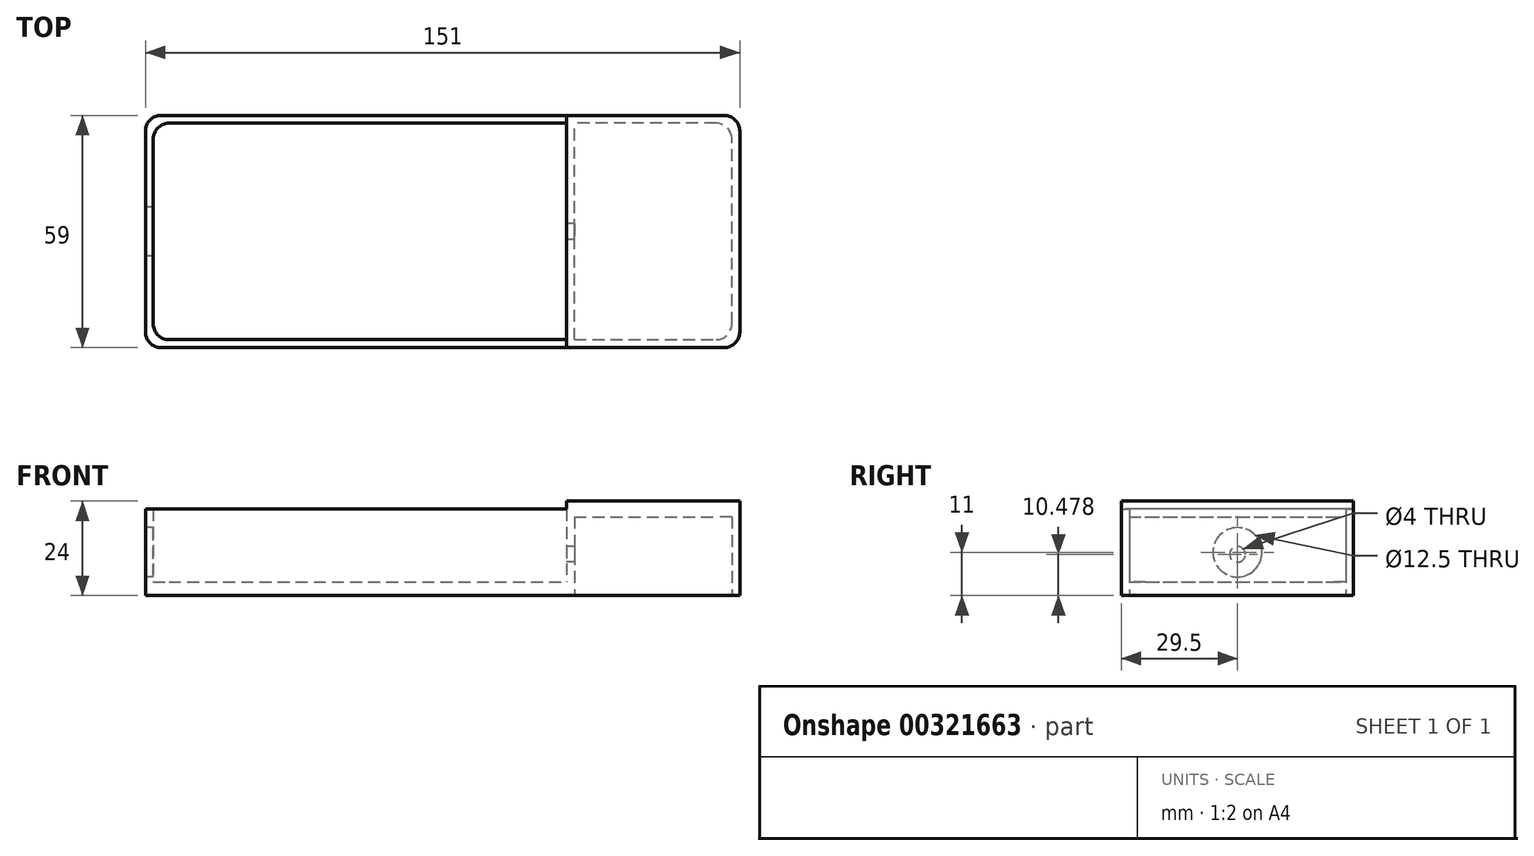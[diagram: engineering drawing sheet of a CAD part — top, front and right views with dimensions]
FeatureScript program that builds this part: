
annotation { "Feature Type Name" : "Feature", "Feature Type Description" : "" }
export const myFeature = defineFeature(function(context is Context, id is Id, definition is map)
    precondition{}
    {
        {
            var Q0;
            Q0=qCreatedBy(makeId("Top.planeOp"),FACE);
            var sketch = newSketch(context, id + "F0", { "sketchPlane" : qUnion([Q0])});
            skLineSegment(sketch, "E0.bottom", {"start": v(65.5, 29.5) * mm, "end": v(-65.5, 29.5) * mm});
            skLineSegment(sketch, "E0.top", {"start": v(65.5, -29.5) * mm, "end": v(-65.5, -29.5) * mm});
            skLineSegment(sketch, "E0.left", {"start": v(65.5, 29.5) * mm, "end": v(65.5, -29.5) * mm});
            skLineSegment(sketch, "E0.right", {"start": v(-65.5, 29.5) * mm, "end": v(-65.5, -29.5) * mm});
            skPoint(sketch, "E0.middle", {"position": v(0, 0) * mm});
            skLineSegment(sketch, "E1.bottom", {"start": v(-63.5, 27.5) * mm, "end": v(21.5, 27.5) * mm});
            skLineSegment(sketch, "E1.top", {"start": v(-63.5, -27.5) * mm, "end": v(21.5, -27.5) * mm});
            skLineSegment(sketch, "E1.left", {"start": v(-63.5, 27.5) * mm, "end": v(-63.5, -27.5) * mm});
            skLineSegment(sketch, "E1.right", {"start": v(21.5, 27.5) * mm, "end": v(21.5, -27.5) * mm});
            skLineSegment(sketch, "E2.bottom", {"start": v(63.5, 27.5) * mm, "end": v(23.5, 27.5) * mm});
            skLineSegment(sketch, "E2.top", {"start": v(63.5, -27.5) * mm, "end": v(23.5, -27.5) * mm});
            skLineSegment(sketch, "E2.left", {"start": v(63.5, 27.5) * mm, "end": v(63.5, -27.5) * mm});
            skLineSegment(sketch, "E2.right", {"start": v(23.5, 27.5) * mm, "end": v(23.5, -27.5) * mm});
            skSolve(sketch);
        }
        {
            var Q0;
            Q0=makeQuery(id+"F0.imprint","IMPRINT",FACE,{"disambiguationData":[TD([[makeQuery(id+"F0.imprint","IMPRINT",EDGE,{"derivedFrom":sQuery(id+"F0.wireOp",EDGE,"E0.bottom")}),1.0]])]});
            extrude(context, id + "F1", {"entities" : qUnion([Q0]), "depth" : 22 * mm});
        }
        {
            var Q0;
            Q0=makeQuery(id+"F1.opExtrude","SWEPT_FACE",FACE,{"disambiguationData":[OSD([sQuery(id+"F0.wireOp",EDGE,"E2.bottom")])]});
            var sketch = newSketch(context, id + "F2", { "sketchPlane" : qUnion([Q0])});
            skLineSegment(sketch, "E3.bottom", {"start": v(23.5, 22) * mm, "end": v(63.5, 22) * mm});
            skLineSegment(sketch, "E3.top", {"start": v(23.5, 20) * mm, "end": v(63.5, 20) * mm});
            skLineSegment(sketch, "E3.left", {"start": v(23.5, 22) * mm, "end": v(23.5, 20) * mm});
            skLineSegment(sketch, "E3.right", {"start": v(63.5, 22) * mm, "end": v(63.5, 20) * mm});
            skSolve(sketch);
        }
        {
            var Q0;
            Q0=makeQuery(id+"F2.imprint","IMPRINT",FACE,{"disambiguationData":[TD([[makeQuery(id+"F2.imprint","IMPRINT",EDGE,{"derivedFrom":sQuery(id+"F2.wireOp",EDGE,"E3.bottom")}),1.0]])]});
            extrude(context, id + "F3", {"entities" : qUnion([Q0]), "operationType" : NewBodyOperationType.ADD, "depth" : 55 * mm});
        }
        {
            var Q0;
            Q0=makeQuery(id+"F1.opExtrude","SWEPT_FACE",FACE,{"disambiguationData":[OSD([sQuery(id+"F0.wireOp",EDGE,"E1.bottom")])]});
            var sketch = newSketch(context, id + "F4", { "sketchPlane" : qUnion([Q0])});
            skLineSegment(sketch, "E4.bottom", {"start": v(-63.5, 0) * mm, "end": v(21.5, 0) * mm});
            skLineSegment(sketch, "E4.top", {"start": v(-63.5, 3.48) * mm, "end": v(21.5, 3.48) * mm});
            skLineSegment(sketch, "E4.left", {"start": v(-63.5, 0) * mm, "end": v(-63.5, 3.48) * mm});
            skLineSegment(sketch, "E4.right", {"start": v(21.5, 0) * mm, "end": v(21.5, 3.48) * mm});
            skSolve(sketch);
        }
        {
            var Q0;
            Q0 = qSketchRegion(id + "F4", true);
            extrude(context, id + "F5", {"entities" : qUnion([Q0]), "operationType" : NewBodyOperationType.ADD, "depth" : 55 * mm});
        }
        {
            var Q0;
            Q0=makeQuery(id+"F3.boolean.opBoolean","MERGE",FACE,{"derivedFrom":[makeQuery(id+"F1.opExtrude","CAP_FACE",FACE,{"disambiguationData":[OSD([sQuery(id+"F0.wireOp",EDGE,"E0.bottom"),sQuery(id+"F0.wireOp",EDGE,"E0.top"),sQuery(id+"F0.wireOp",EDGE,"E0.left"),sQuery(id+"F0.wireOp",EDGE,"E0.right"),sQuery(id+"F0.wireOp",EDGE,"E1.bottom"),sQuery(id+"F0.wireOp",EDGE,"E1.top"),sQuery(id+"F0.wireOp",EDGE,"E1.left"),sQuery(id+"F0.wireOp",EDGE,"E1.right"),sQuery(id+"F0.wireOp",EDGE,"E2.bottom"),sQuery(id+"F0.wireOp",EDGE,"E2.top"),sQuery(id+"F0.wireOp",EDGE,"E2.left"),sQuery(id+"F0.wireOp",EDGE,"E2.right")])],"isStart":false}),makeQuery(id+"F3.opExtrude","SWEPT_FACE",FACE,{"disambiguationData":[OSD([sQuery(id+"F2.wireOp",EDGE,"E3.bottom")])]})]});
            var sketch = newSketch(context, id + "F6", { "sketchPlane" : qUnion([Q0])});
            skLineSegment(sketch, "E5.bottom", {"start": v(65.5, -29.5) * mm, "end": v(21.5, -29.5) * mm});
            skLineSegment(sketch, "E5.top", {"start": v(65.5, 29.5) * mm, "end": v(21.5, 29.5) * mm});
            skLineSegment(sketch, "E5.left", {"start": v(65.5, -29.5) * mm, "end": v(65.5, 29.5) * mm});
            skLineSegment(sketch, "E5.right", {"start": v(21.5, -29.5) * mm, "end": v(21.5, 29.5) * mm});
            skSolve(sketch);
        }
        {
            var Q0;
            {var subQ2=sQuery(id+"F6.wireOp",EDGE,"E5.bottom");Q0=makeQuery(id+"F6.imprint","IMPRINT",FACE,{"disambiguationData":[TD([[makeQuery(id+"F6.imprint","IMPRINT",EDGE,{"derivedFrom":subQ2}),-1.0]])]});}
            extrude(context, id + "F7", {"entities" : qUnion([Q0]), "operationType" : NewBodyOperationType.ADD, "depth" : 2 * mm});
        }
        {
            var Q0;
            Q0=makeQuery(id+"F7.boolean.opBoolean","MERGE",FACE,{"derivedFrom":[makeQuery(id+"F1.opExtrude","SWEPT_FACE",FACE,{"disambiguationData":[OSD([sQuery(id+"F0.wireOp",EDGE,"E1.right")])]}),makeQuery(id+"F7.opExtrude","SWEPT_FACE",FACE,{"disambiguationData":[OSD([sQuery(id+"F6.wireOp",EDGE,"E5.right")])]})]});
            var sketch = newSketch(context, id + "F8", { "sketchPlane" : qUnion([Q0])});
            skCircle(sketch, "E6", {"center": v(0, 10.48) * mm, "radius": 2 * mm});
            skSolve(sketch);
        }
        {
            var Q0;
            Q0=makeQuery(id+"F8.imprint","IMPRINT",FACE,{"disambiguationData":[TD([[makeQuery(id+"F8.imprint","IMPRINT",EDGE,{"derivedFrom":sQuery(id+"F8.wireOp",EDGE,"E6")}),1.0]])]});
            extrude(context, id + "F9", {"entities" : qUnion([Q0]), "operationType" : NewBodyOperationType.REMOVE, "oppositeDirection" : true, "depth" : 2 * mm});
        }
        {
            var Q0;
            Q0=makeQuery(id+"F7.boolean.opBoolean","MERGE",EDGE,{"derivedFrom":[makeQuery(id+"F1.opExtrude","SWEPT_EDGE",EDGE,{"disambiguationData":[OSD([sQuery(id+"F0.wireOp",EDGE,"E0.top"),sQuery(id+"F0.wireOp",EDGE,"E0.left")])]}),makeQuery(id+"F7.opExtrude","SWEPT_EDGE",EDGE,{"disambiguationData":[OSD([sQuery(id+"F6.wireOp",EDGE,"E5.bottom"),sQuery(id+"F6.wireOp",EDGE,"E5.left")])]})]});
            var Q1;
            Q1=makeQuery(id+"F7.boolean.opBoolean","MERGE",EDGE,{"derivedFrom":[makeQuery(id+"F1.opExtrude","SWEPT_EDGE",EDGE,{"disambiguationData":[OSD([sQuery(id+"F0.wireOp",EDGE,"E0.bottom"),sQuery(id+"F0.wireOp",EDGE,"E0.left")])]}),makeQuery(id+"F7.opExtrude","SWEPT_EDGE",EDGE,{"disambiguationData":[OSD([sQuery(id+"F6.wireOp",EDGE,"E5.top"),sQuery(id+"F6.wireOp",EDGE,"E5.left")])]})]});
            var Q2;
            Q2=makeQuery(id+"F1.opExtrude","SWEPT_EDGE",EDGE,{"disambiguationData":[OSD([sQuery(id+"F0.wireOp",EDGE,"E2.top"),sQuery(id+"F0.wireOp",EDGE,"E2.left")])]});
            var Q3;
            Q3=makeQuery(id+"F1.opExtrude","SWEPT_EDGE",EDGE,{"disambiguationData":[OSD([sQuery(id+"F0.wireOp",EDGE,"E2.bottom"),sQuery(id+"F0.wireOp",EDGE,"E2.left")])]});
            fillet(context, id + "F10", {"entities" : qUnion([Q0, Q1, Q2, Q3]), "radius" : 4 * mm, "tangentPropagation" : true, "allowEdgeOverflow" : false});
        }
        {
            var Q0;
            Q0=makeQuery(id+"F1.opExtrude","SWEPT_FACE",FACE,{"disambiguationData":[OSD([sQuery(id+"F0.wireOp",EDGE,"E0.right")])]});
            extrude(context, id + "F11", {"entities" : qUnion([Q0]), "operationType" : NewBodyOperationType.ADD, "depth" : 20 * mm});
        }
        {
            var Q0;
            Q0=makeQuery(id+"F1.opExtrude","SWEPT_FACE",FACE,{"disambiguationData":[OSD([sQuery(id+"F0.wireOp",EDGE,"E1.left")])]});
            extrude(context, id + "F12", {"entities" : qUnion([Q0]), "operationType" : NewBodyOperationType.REMOVE, "oppositeDirection" : true, "depth" : 20 * mm});
        }
        {
            var Q0;
            Q0=makeQuery(id+"F12.boolean.opBoolean","COPY",EDGE,{"derivedFrom":makeQuery(id+"F12.opExtrude","CAP_EDGE",EDGE,{"disambiguationData":[OSD([sQuery(id+"F0.wireOp",EDGE,"E1.bottom"),sQuery(id+"F0.wireOp",EDGE,"E1.left")])],"isStart":false})});
            var Q1;
            Q1=makeQuery(id+"F11.opExtrude","CAP_EDGE",EDGE,{"disambiguationData":[OSD([sQuery(id+"F0.wireOp",EDGE,"E0.top"),sQuery(id+"F0.wireOp",EDGE,"E0.right")])],"isStart":false});
            var Q2;
            Q2=makeQuery(id+"F12.boolean.opBoolean","COPY",EDGE,{"derivedFrom":makeQuery(id+"F12.opExtrude","CAP_EDGE",EDGE,{"disambiguationData":[OSD([sQuery(id+"F0.wireOp",EDGE,"E1.top"),sQuery(id+"F0.wireOp",EDGE,"E1.left")])],"isStart":false})});
            var Q3;
            Q3=makeQuery(id+"F11.opExtrude","CAP_EDGE",EDGE,{"disambiguationData":[OSD([sQuery(id+"F0.wireOp",EDGE,"E0.bottom"),sQuery(id+"F0.wireOp",EDGE,"E0.right")])],"isStart":false});
            fillet(context, id + "F13", {"entities" : qUnion([Q0, Q1, Q2, Q3]), "radius" : 4 * mm, "tangentPropagation" : true, "allowEdgeOverflow" : false});
        }
        {
            var Q0;
            Q0=makeQuery(id+"F11.opExtrude","CAP_FACE",FACE,{"disambiguationData":[OSD([sQuery(id+"F0.wireOp",EDGE,"E0.right")])],"isStart":false});
            var sketch = newSketch(context, id + "F14", { "sketchPlane" : qUnion([Q0])});
            skCircle(sketch, "E7", {"center": v(0, 11) * mm, "radius": 6.25 * mm});
            skSolve(sketch);
        }
        {
            var Q0;
            Q0=makeQuery(id+"F14.imprint","IMPRINT",FACE,{"disambiguationData":[TD([[makeQuery(id+"F14.imprint","IMPRINT",EDGE,{"derivedFrom":sQuery(id+"F14.wireOp",EDGE,"E7")}),1.0]])]});
            extrude(context, id + "F15", {"entities" : qUnion([Q0]), "operationType" : NewBodyOperationType.REMOVE, "oppositeDirection" : true, "depth" : 25 * mm});
        }
    });
